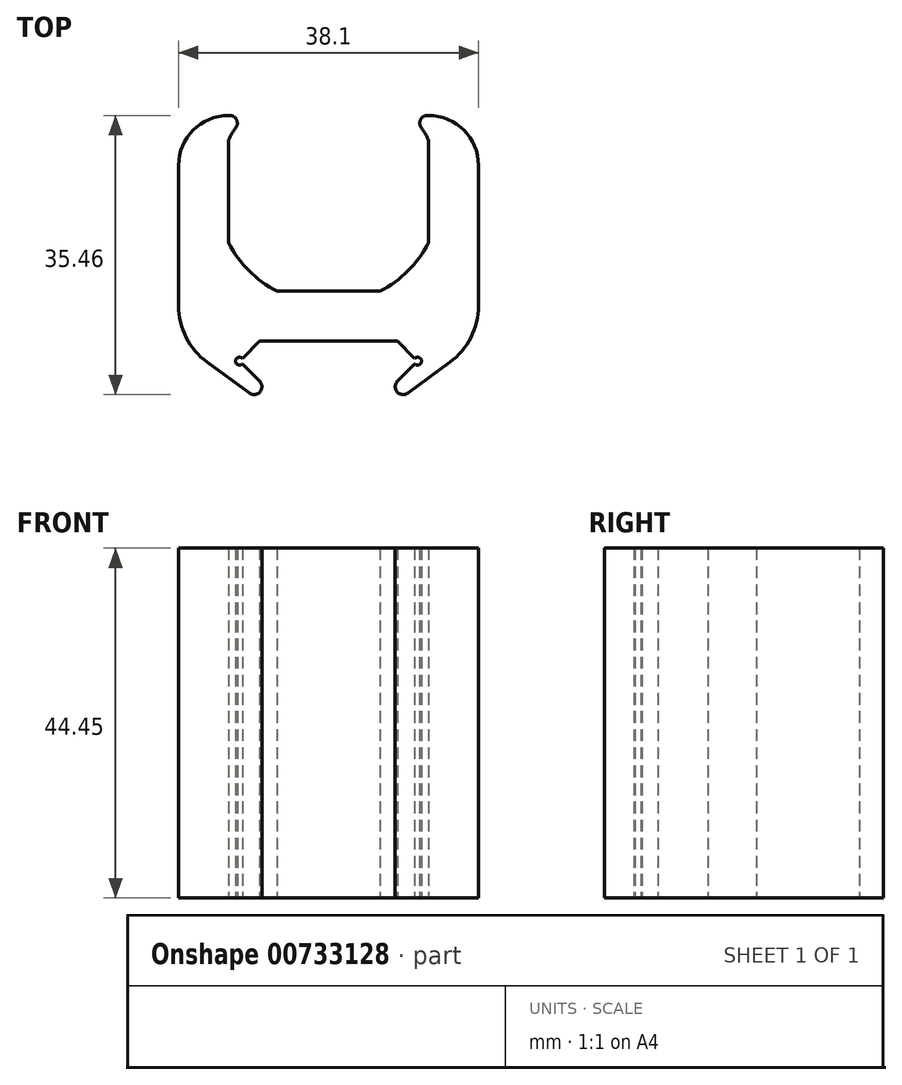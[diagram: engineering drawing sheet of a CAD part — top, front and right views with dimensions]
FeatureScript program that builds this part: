
annotation { "Feature Type Name" : "Feature", "Feature Type Description" : "" }
export const myFeature = defineFeature(function(context is Context, id is Id, definition is map)
    precondition{}
    {
        {
            var Q0;
            Q0=qCreatedBy(makeId("Top.planeOp"),FACE);
            var sketch = newSketch(context, id + "F0", { "sketchPlane" : qUnion([Q0])});
            skLineSegment(sketch, "E0.top", {"start": v(-8.76, -19.05) * mm, "end": v(8.76, -19.05) * mm});
            skLineSegment(sketch, "E0.left", {"start": v(-19.05, 3.27) * mm, "end": v(-19.05, -14.55) * mm});
            skLineSegment(sketch, "E0.right", {"start": v(19.05, 3.27) * mm, "end": v(19.05, -14.55) * mm});
            skPoint(sketch, "E0.middle", {"position": v(0, 0) * mm});
            skLineSegment(sketch, "E1.top", {"start": v(-10.95, -21.24) * mm, "end": v(-8.76, -19.05) * mm});
            skLineSegment(sketch, "E1.left", {"start": v(-8.76, -24.13) * mm, "end": v(-10.95, -21.94) * mm});
            skLineSegment(sketch, "E2.top", {"start": v(8.76, -19.05) * mm, "end": v(10.95, -21.24) * mm});
            skLineSegment(sketch, "E2.right", {"start": v(8.76, -24.13) * mm, "end": v(10.95, -21.94) * mm});
            skArc(sketch, "E3", {"start": v(-10.95, -21.24) * mm, "mid": v(-11.8, -21.6) * mm, "end": v(-10.95, -21.94) * mm});
            skArc(sketch, "E4", {"start": v(10.95, -21.94) * mm, "mid": v(11.8, -21.6) * mm, "end": v(10.95, -21.24) * mm});
            skArc(sketch, "E5", {"start": v(-10.06, -25.64) * mm, "mid": v(-8.71, -25.49) * mm, "end": v(-8.76, -24.13) * mm});
            skArc(sketch, "E6", {"start": v(8.76, -24.13) * mm, "mid": v(8.71, -25.49) * mm, "end": v(10.06, -25.64) * mm});
            skPoint(sketch, "E7.1.start.orphan", {"position": v(-10.18, -25.54) * mm});
            skPoint(sketch, "E8.orphan", {"position": v(10.18, -25.54) * mm});
            skLineSegment(sketch, "E9", {"start": v(-15.42, -21.71) * mm, "end": v(-10.06, -25.64) * mm});
            skLineSegment(sketch, "E10", {"start": v(15.42, -21.71) * mm, "end": v(10.06, -25.64) * mm});
            skArc(sketch, "E11", {"start": v(-12.7, -6.55) * mm, "mid": v(-10.1, -10.1) * mm, "end": v(-6.55, -12.7) * mm});
            skLineSegment(sketch, "E12.top", {"start": v(6.55, -12.7) * mm, "end": v(-6.55, -12.7) * mm});
            skLineSegment(sketch, "E12.left", {"start": v(12.7, 6.55) * mm, "end": v(12.7, -6.55) * mm});
            skLineSegment(sketch, "E12.right", {"start": v(-12.7, 6.55) * mm, "end": v(-12.7, -6.55) * mm});
            skArc(sketch, "E13.trimOffspring", {"start": v(12.7, 6.55) * mm, "mid": v(12.25, 7.35) * mm, "end": v(11.75, 8.13) * mm});
            skArc(sketch, "E14.trimOffspring", {"start": v(6.55, -12.7) * mm, "mid": v(10.1, -10.1) * mm, "end": v(12.7, -6.55) * mm});
            skPoint(sketch, "E15.orphan", {"position": v(-12.7, -12.7) * mm});
            skPoint(sketch, "E16.orphan", {"position": v(12.7, -12.7) * mm});
            skPoint(sketch, "E17.orphan", {"position": v(12.7, 12.7) * mm});
            skArc(sketch, "E18.trimOffspring", {"start": v(-11.75, 8.13) * mm, "mid": v(-12.25, 7.35) * mm, "end": v(-12.7, 6.55) * mm});
            skPoint(sketch, "E19.orphan", {"position": v(-12.7, 12.7) * mm});
            skLineSegment(sketch, "E20", {"start": v(-12.7, 9.62) * mm, "end": v(-12.53, 9.62) * mm});
            skPoint(sketch, "E0.bottom.start.orphan", {"position": v(-19.05, 19.05) * mm});
            skPoint(sketch, "E21.orphan", {"position": v(19.05, 19.05) * mm});
            skPoint(sketch, "E22.orphan", {"position": v(-25.03, 12.7) * mm});
            skPoint(sketch, "E23.end.orphan", {"position": v(-25.03, 6.55) * mm});
            skPoint(sketch, "E23.start.orphan", {"position": v(-25.03, 9.62) * mm});
            skLineSegment(sketch, "E24.trimOffspring", {"start": v(12.53, 9.62) * mm, "end": v(12.7, 9.62) * mm});
            skPoint(sketch, "E25.visualSharp", {"position": v(-10.56, 9.62) * mm});
            skArc(sketch, "E25.filletArc", {"start": v(-11.75, 8.13) * mm, "mid": v(-11.69, 9.11) * mm, "end": v(-12.53, 9.62) * mm});
            skPoint(sketch, "E26.visualSharp", {"position": v(10.56, 9.62) * mm});
            skArc(sketch, "E26.filletArc", {"start": v(12.53, 9.62) * mm, "mid": v(11.69, 9.11) * mm, "end": v(11.75, 8.13) * mm});
            skPoint(sketch, "E27.visualSharp", {"position": v(-19.05, 9.62) * mm});
            skArc(sketch, "E27.filletArc", {"start": v(-12.7, 9.62) * mm, "mid": v(-17.2, 7.76) * mm, "end": v(-19.05, 3.27) * mm});
            skPoint(sketch, "E28.visualSharp", {"position": v(19.05, 9.62) * mm});
            skArc(sketch, "E28.filletArc", {"start": v(19.05, 3.27) * mm, "mid": v(17.2, 7.76) * mm, "end": v(12.7, 9.62) * mm});
            skPoint(sketch, "E29.visualSharp", {"position": v(-19.05, -19.05) * mm});
            skArc(sketch, "E29.filletArc", {"start": v(-19.05, -14.55) * mm, "mid": v(-18.1, -18.56) * mm, "end": v(-15.42, -21.71) * mm});
            skPoint(sketch, "E30.visualSharp", {"position": v(19.05, -19.05) * mm});
            skArc(sketch, "E30.filletArc", {"start": v(15.42, -21.71) * mm, "mid": v(18.1, -18.56) * mm, "end": v(19.05, -14.55) * mm});
            skSolve(sketch);
        }
        {
            var Q0;
            Q0 = qSketchRegion(id + "F0", true);
            extrude(context, id + "F1", {"entities" : qUnion([Q0]), "depth" : 44.45 * mm, "offsetDistance" : 25.4 * mm});
        }
    });
